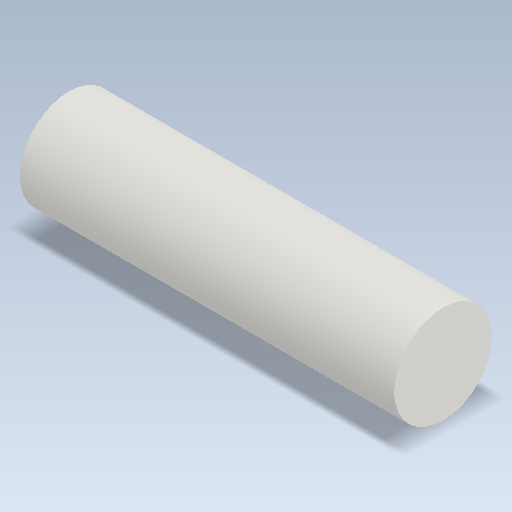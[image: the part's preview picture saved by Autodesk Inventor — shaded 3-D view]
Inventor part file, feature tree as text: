
AUTODESK INVENTOR PART (.ipt)
format: ipt  version: 2021 (Build 250183000, 183)  size: 120,832 bytes
history: native  units: mm
features: other x1, extrude x1, sketch x1
ambient origin geometry x8: Origin, YZ Plane, XZ Plane, XY Plane, X Axis, Y Axis, Z Axis, Center Point
bodies: Body1 (feature_tree)
feature tree (3):
  other  "Sólido1"
  extrude  "Extrusión1"  TaperAngle=0.0deg  [1 undecoded]
  sketch  "Boceto1"  dims[d0=8.8mm d1=0.0mm d2=2.3mm]
note: 1 required parameter value undecoded (feature->parameter linkage not recoverable at this tier; creation-order binding heuristic only, values carry confidence <= 0.55)
